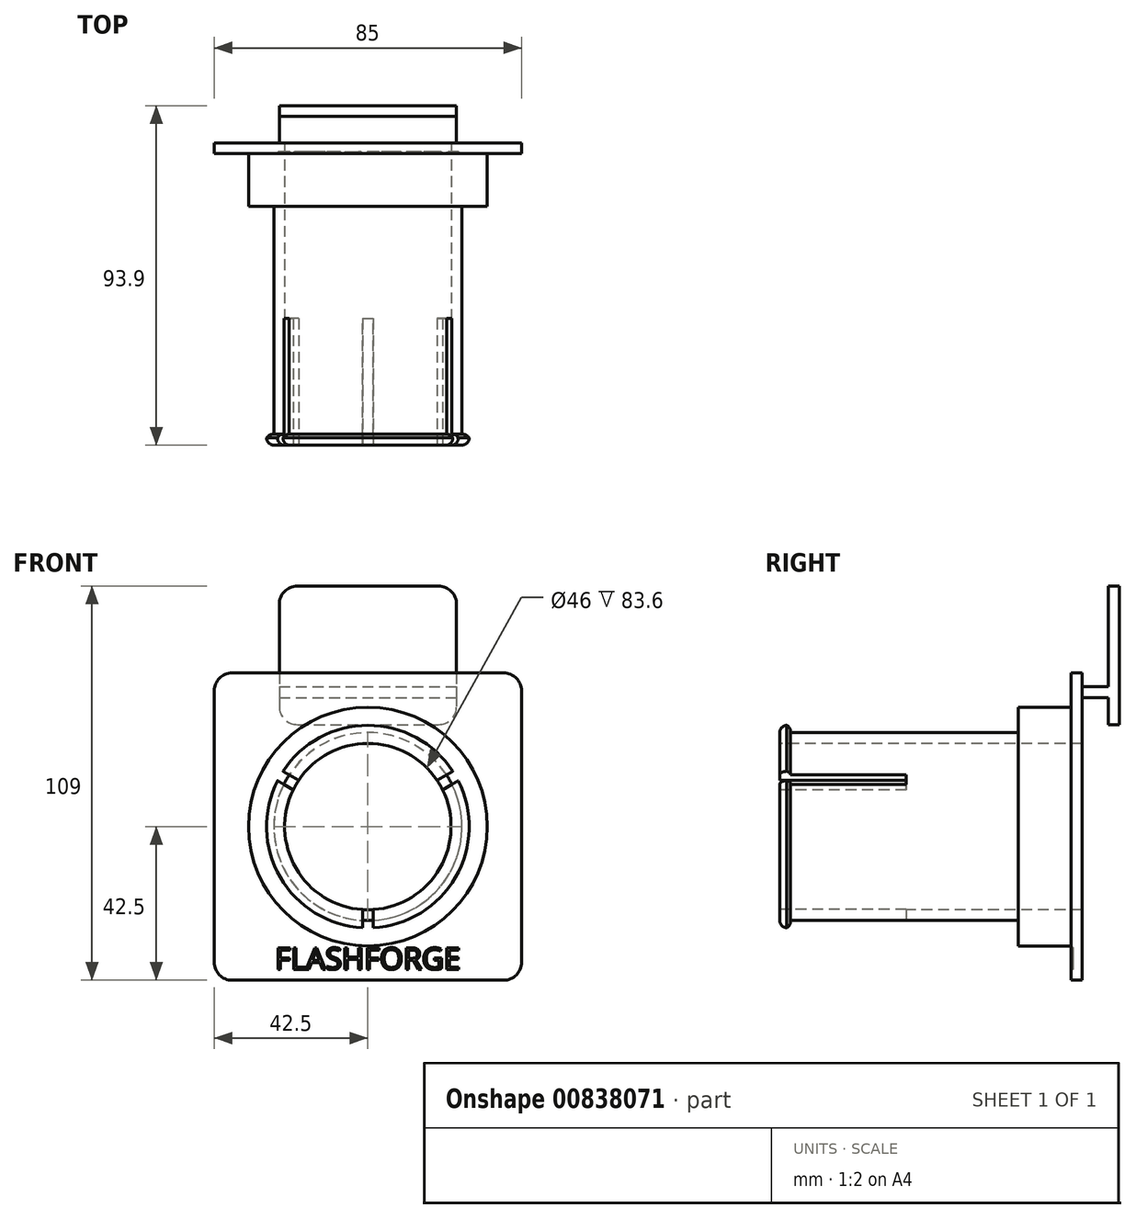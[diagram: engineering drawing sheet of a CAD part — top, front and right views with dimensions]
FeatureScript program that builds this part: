
annotation { "Feature Type Name" : "Feature", "Feature Type Description" : "" }
export const myFeature = defineFeature(function(context is Context, id is Id, definition is map)
    precondition{}
    {
        {
            assignVariable(context, id + "F0", {"name" : "BaseRingHeight", "anyValue" : 14.6});
        }
        {
            assignVariable(context, id + "F1", {"name" : "SpoolRingHeight", "anyValue" : 63});
        }
        {
            var Q0;
            Q0=qCreatedBy(makeId("Front.planeOp"),FACE);
            var sketch = newSketch(context, id + "F2", { "sketchPlane" : qUnion([Q0])});
            skLineSegment(sketch, "E0.bottom", {"start": v(-44, 38.3) * mm, "end": v(-5, 38.3) * mm});
            skLineSegment(sketch, "E0.top", {"start": v(-44, 0) * mm, "end": v(-5, 0) * mm});
            skLineSegment(sketch, "E0.left", {"start": v(-49, 33.3) * mm, "end": v(-49, 5) * mm});
            skLineSegment(sketch, "E0.right", {"start": v(0, 33.3) * mm, "end": v(0, 5) * mm});
            skPoint(sketch, "E1.visualSharp", {"position": v(-49, 38.3) * mm});
            skArc(sketch, "E1.filletArc", {"start": v(-44, 38.3) * mm, "mid": v(-47.54, 36.84) * mm, "end": v(-49, 33.3) * mm});
            skPoint(sketch, "E2.visualSharp", {"position": v(0, 38.3) * mm});
            skArc(sketch, "E2.filletArc", {"start": v(0, 33.3) * mm, "mid": v(-1.46, 36.84) * mm, "end": v(-5, 38.3) * mm});
            skPoint(sketch, "E3.visualSharp", {"position": v(0, 0) * mm});
            skArc(sketch, "E3.filletArc", {"start": v(-5, 0) * mm, "mid": v(-1.46, 1.46) * mm, "end": v(0, 5) * mm});
            skPoint(sketch, "E4.visualSharp", {"position": v(-49, 0) * mm});
            skArc(sketch, "E4.filletArc", {"start": v(-49, 5) * mm, "mid": v(-47.54, 1.46) * mm, "end": v(-44, 0) * mm});
            skSolve(sketch);
        }
        {
            var Q0;
            Q0=qSketchRegion(id+"F2",true);
            extrude(context, id + "F3", {"entities" : qUnion([Q0]), "depth" : 3 * mm, "offsetDistance" : 25 * mm});
        }
        {
            var Q0;
            Q0=makeQuery(id+"F3.opExtrude","CAP_FACE",FACE,{"disambiguationData":[OSD([sQuery(id+"F2.wireOp",EDGE,"E0.bottom"),sQuery(id+"F2.wireOp",EDGE,"E0.top"),sQuery(id+"F2.wireOp",EDGE,"E0.left"),sQuery(id+"F2.wireOp",EDGE,"E0.right")])],"isStart":false});
            var sketch = newSketch(context, id + "F4", { "sketchPlane" : qUnion([Q0])});
            skLineSegment(sketch, "E5.bottom", {"start": v(-49, 10.5) * mm, "end": v(0, 10.5) * mm});
            skLineSegment(sketch, "E5.top", {"start": v(-49, 7.5) * mm, "end": v(0, 7.5) * mm});
            skLineSegment(sketch, "E5.left", {"start": v(-49, 10.5) * mm, "end": v(-49, 7.5) * mm});
            skLineSegment(sketch, "E5.right", {"start": v(0, 10.5) * mm, "end": v(0, 7.5) * mm});
            skSolve(sketch);
        }
        {
            var Q0;
            Q0=qSketchRegion(id+"F4",true);
            extrude(context, id + "F5", {"entities" : qUnion([Q0]), "operationType" : NewBodyOperationType.ADD, "depth" : 7.3 * mm, "offsetDistance" : 25 * mm});
        }
        {
            var Q0;
            Q0=makeQuery(id+"F5.opExtrude","CAP_FACE",FACE,{"disambiguationData":[OSD([sQuery(id+"F4.wireOp",EDGE,"E5.bottom"),sQuery(id+"F4.wireOp",EDGE,"E5.top"),sQuery(id+"F4.wireOp",EDGE,"E5.left"),sQuery(id+"F4.wireOp",EDGE,"E5.right")])],"isStart":false});
            var sketch = newSketch(context, id + "F6", { "sketchPlane" : qUnion([Q0])});
            skLineSegment(sketch, "E6.bottom", {"start": v(-62, 14.3) * mm, "end": v(13, 14.3) * mm});
            skLineSegment(sketch, "E6.top", {"start": v(-62, -70.7) * mm, "end": v(13, -70.7) * mm});
            skLineSegment(sketch, "E6.left", {"start": v(-67, 9.3) * mm, "end": v(-67, -65.7) * mm});
            skLineSegment(sketch, "E6.right", {"start": v(18, 9.3) * mm, "end": v(18, -65.7) * mm});
            skPoint(sketch, "E7.visualSharp", {"position": v(-67, 14.3) * mm});
            skArc(sketch, "E7.filletArc", {"start": v(-62, 14.3) * mm, "mid": v(-65.54, 12.84) * mm, "end": v(-67, 9.3) * mm});
            skPoint(sketch, "E8.visualSharp", {"position": v(18, 14.3) * mm});
            skArc(sketch, "E8.filletArc", {"start": v(18, 9.3) * mm, "mid": v(16.54, 12.84) * mm, "end": v(13, 14.3) * mm});
            skPoint(sketch, "E9.visualSharp", {"position": v(18, -70.7) * mm});
            skArc(sketch, "E9.filletArc", {"start": v(13, -70.7) * mm, "mid": v(16.54, -69.24) * mm, "end": v(18, -65.7) * mm});
            skPoint(sketch, "E10.visualSharp", {"position": v(-67, -70.7) * mm});
            skArc(sketch, "E10.filletArc", {"start": v(-67, -65.7) * mm, "mid": v(-65.54, -69.24) * mm, "end": v(-62, -70.7) * mm});
            skSolve(sketch);
        }
        {
            var Q0;
            Q0=qSketchRegion(id+"F6",true);
            extrude(context, id + "F7", {"entities" : qUnion([Q0]), "operationType" : NewBodyOperationType.ADD, "depth" : 3 * mm, "offsetDistance" : 25 * mm});
        }
        {
            var Q0;
            Q0=makeQuery(id+"F7.opExtrude","CAP_FACE",FACE,{"disambiguationData":[OSD([sQuery(id+"F6.wireOp",EDGE,"E6.bottom"),sQuery(id+"F6.wireOp",EDGE,"E6.top"),sQuery(id+"F6.wireOp",EDGE,"E6.left"),sQuery(id+"F6.wireOp",EDGE,"E6.right"),sQuery(id+"F6.wireOp",EDGE,"E7.filletArc"),sQuery(id+"F6.wireOp",EDGE,"E8.filletArc"),sQuery(id+"F6.wireOp",EDGE,"E9.filletArc"),sQuery(id+"F6.wireOp",EDGE,"E10.filletArc")])],"isStart":false});
            var sketch = newSketch(context, id + "F8", { "sketchPlane" : qUnion([Q0])});
            skCircle(sketch, "E11", {"center": v(-24.5, -28.2) * mm, "radius": 33 * mm});
            skLineSegment(sketch, "E12", {"start": v(-82.43, -28.2) * mm, "end": v(118.43, -28.2) * mm, "construction": true});
            skLineSegment(sketch, "E13", {"start": v(-24.5, 43.68) * mm, "end": v(-24.5, -185.08) * mm, "construction": true});
            skSolve(sketch);
        }
        {
            var Q0;
            Q0=qSketchRegion(id+"F8",true);
            extrude(context, id + "F9", {"entities" : qUnion([Q0]), "operationType" : NewBodyOperationType.ADD, "depth" : (getVariable(context, 'BaseRingHeight')) * mm, "offsetDistance" : 25 * mm});
        }
        {
            var Q0;
            Q0=makeQuery(id+"F9.opExtrude","CAP_FACE",FACE,{"disambiguationData":[OSD([sQuery(id+"F8.wireOp",EDGE,"E11")])],"isStart":false});
            var sketch = newSketch(context, id + "F10", { "sketchPlane" : qUnion([Q0])});
            skCircle(sketch, "E14", {"center": v(-24.5, -28.2) * mm, "radius": 26 * mm});
            skSolve(sketch);
        }
        {
            var Q0;
            Q0=qSketchRegion(id+"F10",true);
            var Q1;
            Q1=qSketchRegion(id+"F12",true);
            extrude(context, id + "F11", {"entities" : qUnion([Q0, Q1]), "operationType" : NewBodyOperationType.ADD, "depth" : (getVariable(context, 'SpoolRingHeight')) * mm, "offsetDistance" : 25 * mm});
        }
        {
            var Q0;
            Q0=makeQuery(id+"F11.opExtrude","CAP_FACE",FACE,{"disambiguationData":[OSD([sQuery(id+"F10.wireOp",EDGE,"E14")])],"isStart":false});
            var sketch = newSketch(context, id + "F12", { "sketchPlane" : qUnion([Q0])});
            skCircle(sketch, "E15", {"center": v(-24.5, -28.2) * mm, "radius": 23 * mm});
            skSolve(sketch);
        }
        {
            var Q0;
            Q0=qSketchRegion(id+"F12",true);
            var Q1;
            Q1=makeQuery(id+"F7.opExtrude","CAP_FACE",FACE,{"disambiguationData":[OSD([sQuery(id+"F6.wireOp",EDGE,"E6.bottom"),sQuery(id+"F6.wireOp",EDGE,"E6.top"),sQuery(id+"F6.wireOp",EDGE,"E6.left"),sQuery(id+"F6.wireOp",EDGE,"E6.right"),sQuery(id+"F6.wireOp",EDGE,"E7.filletArc"),sQuery(id+"F6.wireOp",EDGE,"E8.filletArc"),sQuery(id+"F6.wireOp",EDGE,"E9.filletArc"),sQuery(id+"F6.wireOp",EDGE,"E10.filletArc")])],"isStart":true});
            extrude(context, id + "F13", {"entities" : qUnion([Q0]), "operationType" : NewBodyOperationType.REMOVE, "endBound" : BoundingType.UP_TO_SURFACE, "oppositeDirection" : true, "depth" : 25 * mm, "endBoundEntityFace" : qUnion([Q1]), "offsetDistance" : 25 * mm});
        }
        {
            var Q0;
            {var subQ0=sQuery(id+"F10.wireOp",EDGE,"E14");Q0=makeQuery(id+"F17.boolean.opBoolean","SPLIT",FACE,{"disambiguationData":[TD([makeQuery(id+"F17.opExtrude","SWEPT_FACE",FACE,{"disambiguationData":[OSD([sQuery(id+"F16.wireOp",EDGE,"E21.left")])]})])],"derivedFrom":makeQuery(id+"F11.opExtrude","CAP_FACE",FACE,{"disambiguationData":[OSD([subQ0])],"isStart":false})});}
            var sketch = newSketch(context, id + "F14", { "sketchPlane" : qUnion([Q0])});
            skCircle(sketch, "E16", {"center": v(-24.5, -28.2) * mm, "radius": 23 * mm});
            skCircle(sketch, "E17", {"center": v(-24.5, -28.2) * mm, "radius": 28 * mm});
            skSolve(sketch);
        }
        {
            var Q0;
            Q0=qSketchRegion(id+"F14",true);
            extrude(context, id + "F15", {"entities" : qUnion([Q0]), "operationType" : NewBodyOperationType.ADD, "depth" : 3 * mm, "offsetDistance" : 25 * mm});
        }
        {
            var Q0;
            Q0=makeQuery(id+"F15.opExtrude","CAP_FACE",FACE,{"disambiguationData":[OSD([sQuery(id+"F14.wireOp",EDGE,"E16"),sQuery(id+"F14.wireOp",EDGE,"E17")])],"isStart":false});
            var sketch = newSketch(context, id + "F16", { "sketchPlane" : qUnion([Q0])});
            skLineSegment(sketch, "E18", {"start": v(-24.5, -28.2) * mm, "end": v(-51, -12.9) * mm, "construction": true});
            skLineSegment(sketch, "E19", {"start": v(-24.5, -28.2) * mm, "end": v(2, -12.9) * mm, "construction": true});
            skLineSegment(sketch, "E20", {"start": v(-24.5, -28.2) * mm, "end": v(-24.5, -58.8) * mm, "construction": true});
            skLineSegment(sketch, "E21.bottom", {"start": v(-26, -28.2) * mm, "end": v(-23, -28.2) * mm});
            skLineSegment(sketch, "E21.top", {"start": v(-26, -58.76) * mm, "end": v(-23, -58.76) * mm});
            skLineSegment(sketch, "E21.left", {"start": v(-26, -28.2) * mm, "end": v(-26, -58.76) * mm});
            skLineSegment(sketch, "E21.right", {"start": v(-23, -28.2) * mm, "end": v(-23, -58.76) * mm});
            skCircle(sketch, "E22", {"center": v(-24.5, -28.2) * mm, "radius": 30.6 * mm, "construction": true});
            skLineSegment(sketch, "E23", {"start": v(1.22, -11.62) * mm, "end": v(2.72, -14.22) * mm});
            skLineSegment(sketch, "E24", {"start": v(2.72, -14.22) * mm, "end": v(-23.75, -29.5) * mm});
            skLineSegment(sketch, "E25", {"start": v(-23.75, -29.5) * mm, "end": v(-25.25, -26.9) * mm});
            skLineSegment(sketch, "E26", {"start": v(-25.25, -26.9) * mm, "end": v(1.22, -11.62) * mm});
            skLineSegment(sketch, "E27", {"start": v(-50.22, -11.62) * mm, "end": v(-51.72, -14.22) * mm});
            skLineSegment(sketch, "E28", {"start": v(-51.72, -14.22) * mm, "end": v(-25.25, -29.5) * mm});
            skLineSegment(sketch, "E29", {"start": v(-25.25, -29.5) * mm, "end": v(-23.75, -26.9) * mm});
            skLineSegment(sketch, "E30", {"start": v(-23.75, -26.9) * mm, "end": v(-50.22, -11.62) * mm});
            skSolve(sketch);
        }
        {
            var Q0;
            Q0=qSketchRegion(id+"F16",true);
            extrude(context, id + "F17", {"entities" : qUnion([Q0]), "operationType" : NewBodyOperationType.REMOVE, "oppositeDirection" : true, "depth" : 70 * mm, "offsetDistance" : 25 * mm, "symmetric" : true});
        }
        {
            var Q0;
            {var subQ0=sQuery(id+"F14.wireOp",EDGE,"E17");Q0=makeQuery(id+"F17.boolean.opBoolean","SPLIT",EDGE,{"disambiguationData":[TD([makeQuery(id+"F17.opExtrude","SWEPT_FACE",FACE,{"disambiguationData":[OSD([sQuery(id+"F16.wireOp",EDGE,"E21.left")])]})])],"derivedFrom":makeQuery(id+"F15.opExtrude","CAP_EDGE",EDGE,{"disambiguationData":[OSD([subQ0])],"isStart":false})});}
            var Q1;
            {var subQ0=sQuery(id+"F14.wireOp",EDGE,"E17");Q1=makeQuery(id+"F17.boolean.opBoolean","SPLIT",EDGE,{"disambiguationData":[TD([makeQuery(id+"F17.opExtrude","SWEPT_FACE",FACE,{"disambiguationData":[OSD([sQuery(id+"F16.wireOp",EDGE,"E26")])]})])],"derivedFrom":makeQuery(id+"F15.opExtrude","CAP_EDGE",EDGE,{"disambiguationData":[OSD([subQ0])],"isStart":false})});}
            var Q2;
            {var subQ0=sQuery(id+"F14.wireOp",EDGE,"E17");Q2=makeQuery(id+"F17.boolean.opBoolean","SPLIT",EDGE,{"disambiguationData":[TD([makeQuery(id+"F17.opExtrude","SWEPT_FACE",FACE,{"disambiguationData":[OSD([sQuery(id+"F16.wireOp",EDGE,"E21.right")])]})])],"derivedFrom":makeQuery(id+"F15.opExtrude","CAP_EDGE",EDGE,{"disambiguationData":[OSD([subQ0])],"isStart":false})});}
            fillet(context, id + "F18", {"entities" : qUnion([Q0, Q1, Q2]), "radius" : 2 * mm, "tangentPropagation" : true, "allowEdgeOverflow" : false});
        }
        {
            var Q0;
            {var subQ0=sQuery(id+"F14.wireOp",EDGE,"E17");Q0=makeQuery(id+"F17.boolean.opBoolean","SPLIT",EDGE,{"disambiguationData":[TD([makeQuery(id+"F17.opExtrude","SWEPT_FACE",FACE,{"disambiguationData":[OSD([sQuery(id+"F16.wireOp",EDGE,"E21.right")])]})])],"derivedFrom":makeQuery(id+"F15.opExtrude","CAP_EDGE",EDGE,{"disambiguationData":[OSD([subQ0])],"isStart":true})});}
            var Q1;
            {var subQ0=sQuery(id+"F14.wireOp",EDGE,"E17");Q1=makeQuery(id+"F17.boolean.opBoolean","SPLIT",EDGE,{"disambiguationData":[TD([makeQuery(id+"F17.opExtrude","SWEPT_FACE",FACE,{"disambiguationData":[OSD([sQuery(id+"F16.wireOp",EDGE,"E26")])]})])],"derivedFrom":makeQuery(id+"F15.opExtrude","CAP_EDGE",EDGE,{"disambiguationData":[OSD([subQ0])],"isStart":true})});}
            var Q2;
            {var subQ0=sQuery(id+"F14.wireOp",EDGE,"E17");Q2=makeQuery(id+"F17.boolean.opBoolean","SPLIT",EDGE,{"disambiguationData":[TD([makeQuery(id+"F17.opExtrude","SWEPT_FACE",FACE,{"disambiguationData":[OSD([sQuery(id+"F16.wireOp",EDGE,"E21.left")])]})])],"derivedFrom":makeQuery(id+"F15.opExtrude","CAP_EDGE",EDGE,{"disambiguationData":[OSD([subQ0])],"isStart":true})});}
            fillet(context, id + "F19", {"entities" : qUnion([Q0, Q1, Q2]), "radius" : 2 * mm, "tangentPropagation" : true, "allowEdgeOverflow" : false});
        }
        {
            var Q0;
            Q0=makeQuery(id+"F8.imprint","IMPRINT",FACE,{"disambiguationData":[TD([[makeQuery(id+"F8.imprint","IMPRINT",EDGE,{"derivedFrom":sQuery(id+"F8.wireOp",EDGE,"E11")}),-1.0]])]});
            var sketch = newSketch(context, id + "F20", { "sketchPlane" : qUnion([Q0])});
            skText(sketch, "E31", { "text": "FLASHFORGE\n", "fontName": "OpenSans-Regular.ttf"});
            skLineSegment(sketch, "E32", {"start": v(14.01, -67.7) * mm, "end": v(-56.31, -67.7) * mm, "construction": true});
            const initialGuessF20  = {"E31": [-0.05015, -0.0677, 1, 0, 0.006]};
            skSetInitialGuess(sketch, initialGuessF20);
            skSolve(sketch);
        }
        {
            var Q0;
            Q0=qSketchRegion(id+"F20",true);
            extrude(context, id + "F21", {"entities" : qUnion([Q0]), "operationType" : NewBodyOperationType.REMOVE, "oppositeDirection" : true, "depth" : .5 * mm, "offsetDistance" : 25 * mm});
        }
    });
